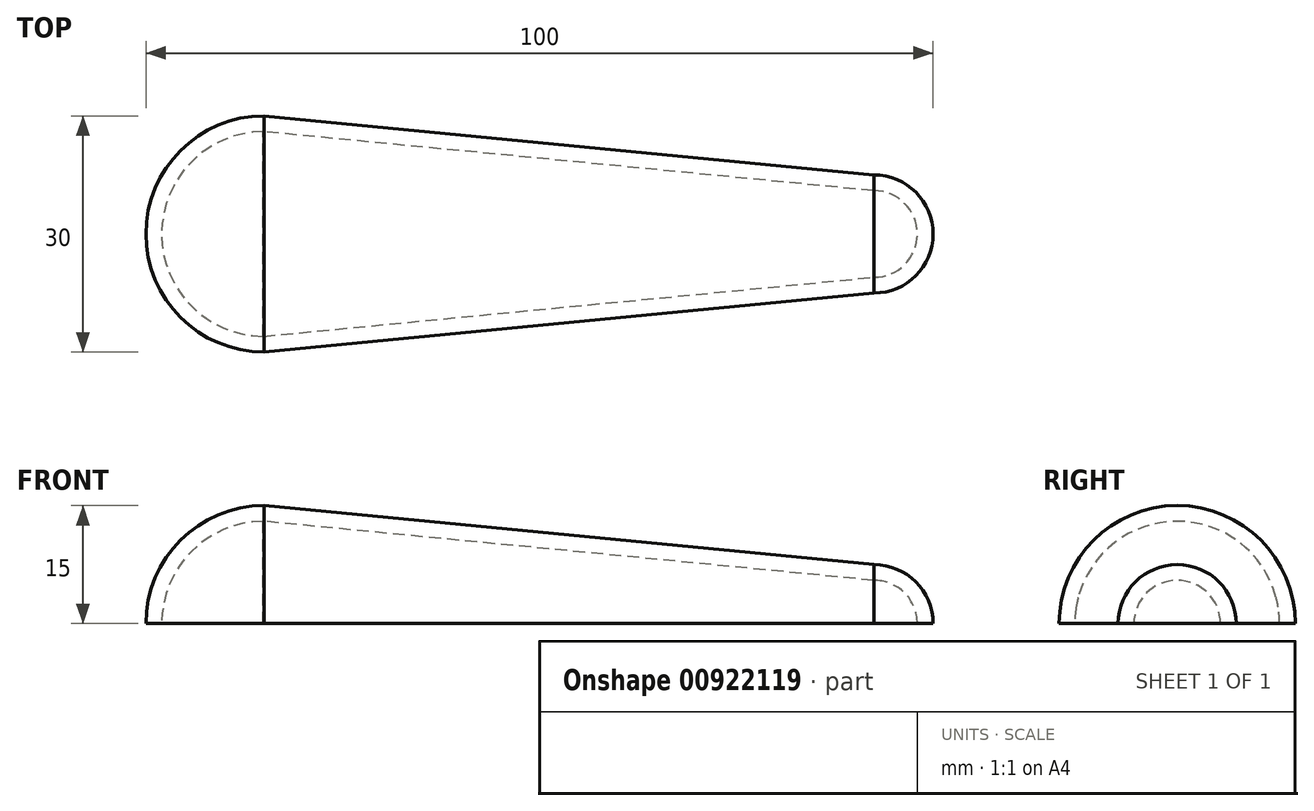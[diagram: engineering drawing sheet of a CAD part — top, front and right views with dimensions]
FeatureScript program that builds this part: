
annotation { "Feature Type Name" : "Feature", "Feature Type Description" : "" }
export const myFeature = defineFeature(function(context is Context, id is Id, definition is map)
    precondition{}
    {
        {
            var Q0;
            Q0=qCreatedBy(makeId("Top.planeOp"),FACE);
            var sketch = newSketch(context, id + "F0", { "sketchPlane" : qUnion([Q0])});
            skArc(sketch, "E0", {"start": v(-33.55, 14.93) * mm, "mid": v(-50, 0) * mm, "end": v(-33.55, -14.93) * mm});
            skArc(sketch, "E1", {"start": v(43.23, -7.46) * mm, "mid": v(50, 0) * mm, "end": v(43.23, 7.46) * mm});
            skLineSegment(sketch, "E2", {"start": v(-33.55, 14.93) * mm, "end": v(43.23, 7.46) * mm});
            skLineSegment(sketch, "E3", {"start": v(-33.55, -14.93) * mm, "end": v(43.23, -7.46) * mm});
            skLineSegment(sketch, "E4", {"start": v(42.5, 28.22) * mm, "end": v(42.5, -28.6) * mm, "construction": true});
            skPoint(sketch, "E4.startSnap0", {"position": v(50, 0) * mm});
            skPoint(sketch, "E4.endSnap0", {"position": v(50, 0) * mm});
            skLineSegment(sketch, "E5", {"start": v(-35, 32.49) * mm, "end": v(-35, -32.49) * mm, "construction": true});
            skPoint(sketch, "E5.startSnap0", {"position": v(-50, 0) * mm});
            skLineSegment(sketch, "E6", {"start": v(42.5, 28.22) * mm, "end": v(42.5, -28.6) * mm});
            skLineSegment(sketch, "E7", {"start": v(-35, 32.49) * mm, "end": v(-35, -32.49) * mm});
            skSolve(sketch);
        }
        {
            var Q0;
            Q0=sQuery(id+"F0.wireOp",EDGE,"E4");
            cPlane(context, id + "F1", {"entities" : qUnion([Q0]), "cplaneType" : CPlaneType.LINE_ANGLE, "offset" : 25 * mm, "angle" : 90 * degree, "width" : 150 * mm, "height" : 150 * mm});
        }
        {
            var Q0;
            Q0=sQuery(id+"F0.wireOp",EDGE,"E5");
            cPlane(context, id + "F2", {"entities" : qUnion([Q0]), "cplaneType" : CPlaneType.LINE_ANGLE, "offset" : 25 * mm, "angle" : 90 * degree, "oppositeDirection" : true, "width" : 150 * mm, "height" : 150 * mm});
        }
        {
            var Q0;
            Q0=qCreatedBy(id+"F1.planeOp",FACE);
            var sketch = newSketch(context, id + "F3", { "sketchPlane" : qUnion([Q0])});
            skArc(sketch, "E8", {"start": v(7.5, 0) * mm, "mid": v(0, 7.5) * mm, "end": v(-7.5, 0) * mm});
            skLineSegment(sketch, "E9", {"start": v(-7.5, 0) * mm, "end": v(7.5, 0) * mm});
            skSolve(sketch);
        }
        {
            var Q0;
            Q0=qCreatedBy(id+"F2.planeOp",FACE);
            var sketch = newSketch(context, id + "F4", { "sketchPlane" : qUnion([Q0])});
            skArc(sketch, "E10", {"start": v(15, 0) * mm, "mid": v(0, 15) * mm, "end": v(-15, 0) * mm});
            skLineSegment(sketch, "E11", {"start": v(-15, 0) * mm, "end": v(15, 0) * mm});
            skSolve(sketch);
        }
        {
            var Q0;
            Q0=makeQuery(id+"F4.imprint","IMPRINT",FACE,{"disambiguationData":[TD([[makeQuery(id+"F4.imprint","IMPRINT",EDGE,{"derivedFrom":sQuery(id+"F4.wireOp",EDGE,"E10")}),1.0]])]});
            var Q1;
            Q1=makeQuery(id+"F3.imprint","IMPRINT",FACE,{"disambiguationData":[TD([[makeQuery(id+"F3.imprint","IMPRINT",EDGE,{"derivedFrom":sQuery(id+"F3.wireOp",EDGE,"E8")}),1.0]])]});
            var Q2;
            Q2=sQuery(id+"F0.wireOp",EDGE,"E2");
            var Q3;
            Q3=sQuery(id+"F0.wireOp",EDGE,"E3");
            loft(context, id + "F5", {"sheetProfilesArray" : [{ "sheetProfileEntities" : qUnion([Q0]) }, { "sheetProfileEntities" : qUnion([Q1]) }], "guidesArray" : [{ "guideEntities" : qUnion([Q2]), "guideDerivativeType" : LoftGuideDerivativeType.DEFAULT, "guideDerivativeMagnitude" : 1 }, { "guideEntities" : qUnion([Q3]), "guideDerivativeType" : LoftGuideDerivativeType.DEFAULT, "guideDerivativeMagnitude" : 1 }]});
        }
        {
            var Q0;
            Q0=makeQuery(id+"F5.opLoft","CAP_FACE",FACE,{"disambiguationData":[OSD([makeQuery(id+"F3.imprint","IMPRINT",FACE,{"disambiguationData":[TD([[makeQuery(id+"F3.imprint","IMPRINT",EDGE,{"derivedFrom":sQuery(id+"F3.wireOp",EDGE,"E8")}),1.0]])]})])],"isStart":true});
            var Q1;
            Q1=sQuery(id+"F0.wireOp",EDGE,"E6");
            revolve(context, id + "F6", {"operationType" : NewBodyOperationType.ADD, "surfaceOperationType" : NewSurfaceOperationType.NEW, "entities" : qUnion([Q0]), "axis" : qUnion([Q1]), "revolveType" : RevolveType.ONE_DIRECTION, "oppositeDirection" : true, "angle" : 90 * degree});
        }
        {
            var Q0;
            Q0=makeQuery(id+"F5.opLoft","CAP_FACE",FACE,{"disambiguationData":[OSD([makeQuery(id+"F4.imprint","IMPRINT",FACE,{"disambiguationData":[TD([[makeQuery(id+"F4.imprint","IMPRINT",EDGE,{"derivedFrom":sQuery(id+"F4.wireOp",EDGE,"E10")}),1.0]])]})])],"isStart":true});
            var Q1;
            Q1=sQuery(id+"F0.wireOp",EDGE,"E7");
            revolve(context, id + "F7", {"operationType" : NewBodyOperationType.ADD, "surfaceOperationType" : NewSurfaceOperationType.NEW, "entities" : qUnion([Q0]), "axis" : qUnion([Q1]), "revolveType" : RevolveType.ONE_DIRECTION, "angle" : 90 * degree});
        }
        {
            var Q0;
            {var subQ0=sQuery(id+"F4.wireOp",EDGE,"E10");var subQ1=sQuery(id+"F4.wireOp",EDGE,"E11");var subQ2=makeQuery(id+"F4.imprint","IMPRINT",EDGE,{"derivedFrom":subQ1});var subQ3=sQuery(id+"F3.wireOp",EDGE,"E8");var subQ4=sQuery(id+"F3.wireOp",EDGE,"E9");var subQ5=makeQuery(id+"F3.imprint","IMPRINT",EDGE,{"derivedFrom":subQ4});Q0=makeQuery(id+"F7.boolean.opBoolean","MERGE",FACE,{"derivedFrom":[makeQuery(id+"F6.boolean.opBoolean","MERGE",FACE,{"derivedFrom":[makeQuery(id+"F5.opLoft","SWEPT_FACE",FACE,{"disambiguationData":[OSD([subQ3,subQ4,subQ0,subQ1]),TDD([makeQuery(id+"F3.imprint","INTERSECT",VERTEX,{"disambiguationData":[OD(0.0)],"derivedFrom":[subQ3,subQ4]}),makeQuery(id+"F3.imprint","INTERSECT",VERTEX,{"disambiguationData":[OD(1.0)],"derivedFrom":[subQ3,subQ4]}),subQ5,makeQuery(id+"F4.imprint","INTERSECT",VERTEX,{"disambiguationData":[OD(0.0)],"derivedFrom":[subQ0,subQ1]}),makeQuery(id+"F4.imprint","INTERSECT",VERTEX,{"disambiguationData":[OD(1.0)],"derivedFrom":[subQ0,subQ1]}),subQ2])]}),makeQuery(id+"F6.opRevolve","CAP_FACE",FACE,{"disambiguationData":[OSD([makeQuery(id+"F3.imprint","IMPRINT",FACE,{"disambiguationData":[TD([[makeQuery(id+"F3.imprint","IMPRINT",EDGE,{"derivedFrom":subQ3}),1.0]])]})])],"isStart":false})]}),makeQuery(id+"F7.opRevolve","CAP_FACE",FACE,{"disambiguationData":[OSD([makeQuery(id+"F4.imprint","IMPRINT",FACE,{"disambiguationData":[TD([[makeQuery(id+"F4.imprint","IMPRINT",EDGE,{"derivedFrom":subQ0}),1.0]])]})])],"isStart":false})]});}
            shell(context, id + "F8", {"entities" : qUnion([Q0]), "thickness" : 2 * mm});
        }
        {
            var Q0;
            Q0=qCreatedBy(makeId("Front.planeOp"),FACE);
            var sketch = newSketch(context, id + "F9", { "sketchPlane" : qUnion([Q0])});
            skLineSegment(sketch, "E12", {"start": v(0, 0) * mm, "end": v(-30, 0) * mm, "construction": true});
            skLineSegment(sketch, "E13", {"start": v(-30, 0) * mm, "end": v(-30, 15) * mm, "construction": true});
            skLineSegment(sketch, "E14", {"start": v(40, 0) * mm, "end": v(40, 7.5) * mm, "construction": true});
            skLineSegment(sketch, "E15", {"start": v(-30, 15) * mm, "end": v(40, 7.5) * mm});
            skSolve(sketch);
        }
    });
